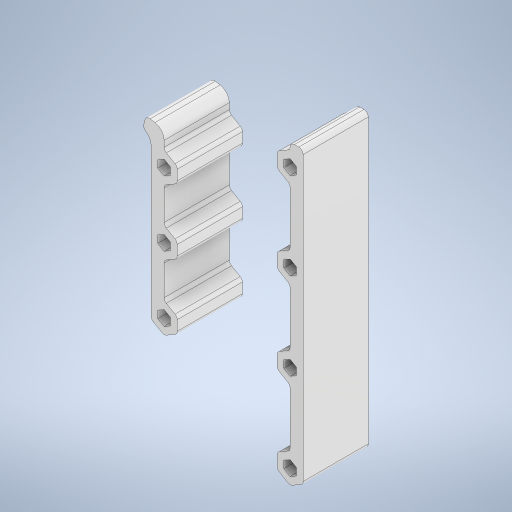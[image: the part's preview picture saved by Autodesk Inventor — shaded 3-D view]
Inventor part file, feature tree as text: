
AUTODESK INVENTOR PART (.ipt)
format: ipt  version: 2024.3 (Build 283343000, 343)  size: 1,198,592 bytes
history: native  units: mm
features: sketch x11, extrude x8, fillet x6, hole x3, projected_geometry x3, other x1
ambient origin geometry x8: Origin, YZ Plane, XZ Plane, XY Plane, X Axis, Y Axis, Z Axis, Center Point
bodies: Body1 (feature_tree)
feature tree (32):
  other  "ソリッド1"
  extrude  "押し出し1"  Depth=120.0mm
  hole  "穴1"  [1 undecoded]
  extrude  "押し出し3"  Depth=92.0mm
  extrude  "押し出し10"  TaperAngle=22.5deg  [1 undecoded]
  hole  "穴8"  [1 undecoded]
  fillet  "フィレット4"  Radius=60.0mm
  hole  "穴13"  [1 undecoded]
  fillet  "フィレット11"  Radius=210.0mm
  extrude  "押し出し17"  Depth=210.0mm
  extrude  "押し出し18"  Depth=3.0mm TaperAngle=0.0deg
  fillet  "フィレット15"  [1 undecoded]
  fillet  "フィレット16"  Radius=14.835299mm
  fillet  "フィレット17"  Radius=14.835299mm
  extrude  "押し出し19"  Depth=60.0mm
  extrude  "押し出し20"  Depth=10.0mm TaperAngle=0.0deg
  fillet  "フィレット18"  Radius=180.0mm
  extrude  "押し出し21"  TaperAngle=45.0deg  [1 undecoded]
  sketch  "スケッチ1"
  sketch  "スケッチ2"
  sketch  "スケッチ4"
  sketch  "スケッチ17"
  sketch  "スケッチ20"
  sketch  "スケッチ28"
  sketch  "スケッチ32"
  sketch  "スケッチ33"
  sketch  "スケッチ34"
  sketch  "スケッチ35"
  projected_geometry  "投影ループ2"
  sketch  "スケッチ36"
  projected_geometry  "投影ループ3"
  projected_geometry  "投影ループ4"
note: 6 required parameter values undecoded (feature->parameter linkage not recoverable at this tier; creation-order binding heuristic only, values carry confidence <= 0.55)
